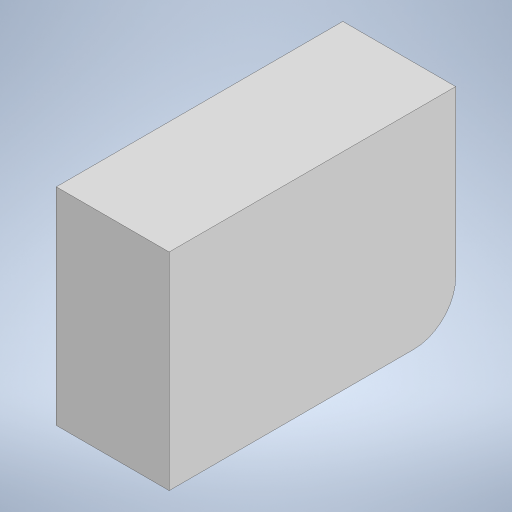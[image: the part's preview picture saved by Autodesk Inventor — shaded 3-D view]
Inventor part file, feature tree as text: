
AUTODESK INVENTOR PART (.ipt)
format: ipt  version: 2023 (Build 270158000, 158)  size: 556,544 bytes
history: native  units: in
note: dims shown in document units (in); Inventor stores cm internally (conversion verified against a paired STEP export)
features: extrude x6, fillet x6, sketch x6, projected_geometry x3, plane x1
ambient origin geometry x8: Origin, YZ Plane, XZ Plane, XY Plane, X Axis, Y Axis, Z Axis, Center Point
bodies: Solid1 (feature_tree)
feature tree (22):
  extrude  "Extrusion1"  Depth=0.1575in
  extrude  "Extrusion2"  Depth=0.7874in
  extrude  "Extrusion3"  Depth=0.1575in
  fillet  "Fillet1"  Radius=0.1575in
  fillet  "Fillet2"  Radius=0.7874in
  fillet  "Fillet3"  Radius=0.1575in
  fillet  "Fillet4"  Radius=0.7874in
  sketch  "Sketch4"  dims[d26=0.7874in d27=0.1575in]
  extrude  "Extrusion4"  Depth=0.1575in
  extrude  "Extrusion5"  Depth=0.1575in
  fillet  "Fillet8"  Radius=0.7874in
  fillet  "Fillet9"  Radius=1.378in
  plane  "Work Plane1"
  sketch  "Sketch6"  dims[d28=0.7874in d30=0.1575in d31=0.7874in d32=1.378in]
  extrude  "Extrusion6"  Depth=0.7874in
  sketch  "Sketch1"  dims[d10=6.4961in d11=0.1575in]
  sketch  "Sketch2"  dims[d12=4.685in d13=0.0in d18=0.7874in]
  sketch  "Sketch3"  dims[d19=0.1575in d20=0.1575in d21=0.1575in d22=0.7874in d24=0.1575in d25=0.7874in]
  projected_geometry  "Projected Loop1"
  projected_geometry  "Projected Loop2"
  sketch  "Sketch7"  dims[d33=0.1575in d34=0.7874in d35=2.2441in d36=0.0in d37=0.1575in d38=0.0in d39=0.0787in d40=0.8661in d41=0.3937in d42=0.3937in d43=1.811in d44=1.811in d45=2.1457in d46=1.2303in d47=2.5591in d48=1.2795in d49=0.1575in d50=0.0in d51=1.6142in d52=1.6142in d53=0.3937in d54=0.0in d58=0.0787in d59=0.9449in d60=-1.2795in d61=0.0394in d62=0.0394in d63=0.0512in d64=0.315in d65=1.378in d66=0.689in d67=0.6299in d68=0.3937in d69=0.0in]
  projected_geometry  "Project Cut Edges1"
